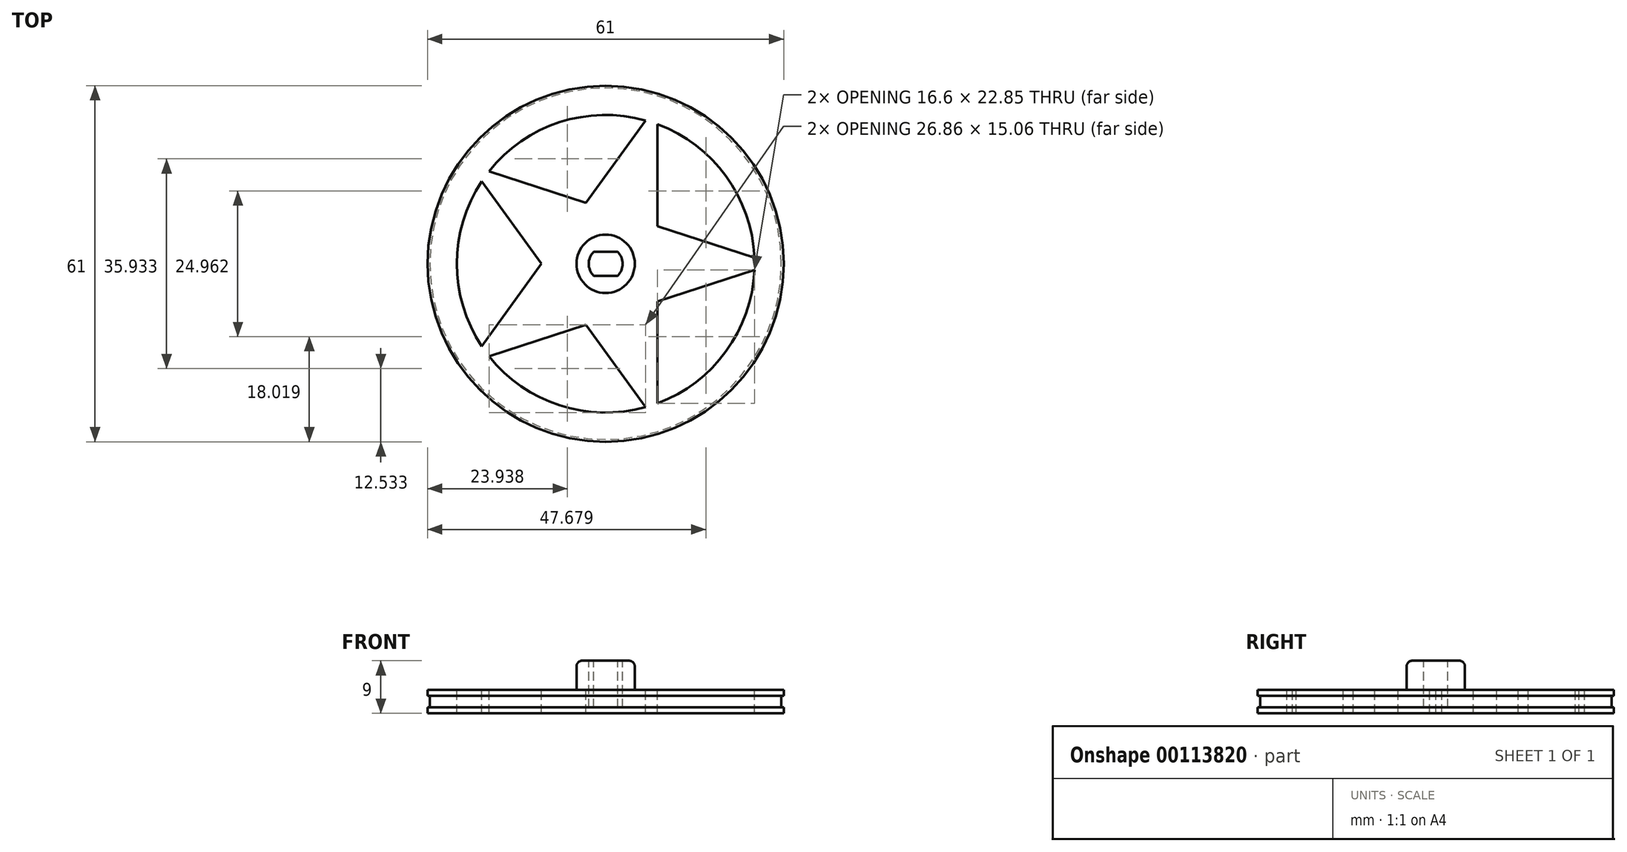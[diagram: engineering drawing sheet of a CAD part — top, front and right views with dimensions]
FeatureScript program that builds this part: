
annotation { "Feature Type Name" : "Feature", "Feature Type Description" : "" }
export const myFeature = defineFeature(function(context is Context, id is Id, definition is map)
    precondition{}
    {
        {
            var Q0;
            Q0=qCreatedBy(makeId("Top.planeOp"),FACE);
            var sketch = newSketch(context, id + "F0", { "sketchPlane" : qUnion([Q0])});
            skCircle(sketch, "E0", {"center": v(0, 0) * mm, "radius": 30.5 * mm});
            skSolve(sketch);
        }
        {
            var Q0;
            Q0 = qSketchRegion(id + "F0", true);
            extrude(context, id + "F1", {"entities" : qUnion([Q0]), "depth" : 4 * mm});
        }
        {
            var Q0;
            Q0=qCreatedBy(makeId("Top.planeOp"),FACE);
            cPlane(context, id + "F2", {"entities" : qUnion([Q0]), "cplaneType" : CPlaneType.OFFSET, "offset" : 1 * mm, "width" : 150 * mm, "height" : 150 * mm});
        }
        {
            var Q0;
            Q0=qCreatedBy(id+"F2.planeOp",FACE);
            var sketch = newSketch(context, id + "F3", { "sketchPlane" : qUnion([Q0])});
            skCircle(sketch, "E1.0", {"center": v(0, 0) * mm, "radius": 30.5 * mm});
            skCircle(sketch, "E2.0", {"center": v(0, 0) * mm, "radius": 30.1 * mm});
            skSolve(sketch);
        }
        {
            var Q0;
            Q0 = qSketchRegion(id + "F3", true);
            extrude(context, id + "F4", {"entities" : qUnion([Q0]), "operationType" : NewBodyOperationType.REMOVE, "depth" : 2 * mm});
        }
        {
            var Q0;
            Q0=makeQuery(id+"F1.opExtrude","CAP_FACE",FACE,{"disambiguationData":[OSD([sQuery(id+"F0.wireOp",EDGE,"E0")])],"isStart":false});
            var sketch = newSketch(context, id + "F5", { "sketchPlane" : qUnion([Q0])});
            skCircle(sketch, "E3", {"center": v(0, 0) * mm, "radius": 5 * mm});
            skSolve(sketch);
        }
        {
            var Q0;
            Q0 = qSketchRegion(id + "F5", true);
            extrude(context, id + "F6", {"entities" : qUnion([Q0]), "operationType" : NewBodyOperationType.ADD, "depth" : 5 * mm});
        }
        {
            var Q0;
            Q0=makeQuery(id+"F6.opExtrude","CAP_FACE",FACE,{"disambiguationData":[OSD([sQuery(id+"F5.wireOp",EDGE,"E3")])],"isStart":false});
            var sketch = newSketch(context, id + "F7", { "sketchPlane" : qUnion([Q0])});
            skArc(sketch, "E4", {"start": v(-2.05, 2.05) * mm, "mid": v(-2.9, 0) * mm, "end": v(-2.05, -2.05) * mm});
            skLineSegment(sketch, "E5", {"start": v(-2.05, 2.05) * mm, "end": v(2.05, 2.05) * mm});
            skLineSegment(sketch, "E6.MirrorCS", {"start": v(-2.05, -2.05) * mm, "end": v(2.05, -2.05) * mm});
            skArc(sketch, "E7.trimOffspring", {"start": v(2.05, -2.05) * mm, "mid": v(2.9, 0) * mm, "end": v(2.05, 2.05) * mm});
            skSolve(sketch);
        }
        {
            var Q0;
            Q0 = qSketchRegion(id + "F7", true);
            var Q1;
            Q1=qCreatedBy(id+"F2.planeOp",FACE);
            extrude(context, id + "F8", {"entities" : qUnion([Q0]), "operationType" : NewBodyOperationType.REMOVE, "endBound" : BoundingType.UP_TO_SURFACE, "oppositeDirection" : true, "endBoundEntityFace" : qUnion([Q1]), "depth" : 25 * mm});
        }
        {
            var Q0;
            Q0=makeQuery(id+"F1.opExtrude","CAP_FACE",FACE,{"disambiguationData":[OSD([sQuery(id+"F0.wireOp",EDGE,"E0")])],"isStart":false});
            var sketch = newSketch(context, id + "F9", { "sketchPlane" : qUnion([Q0])});
            skCircle(sketch, "E8.cCircle", {"center": v(0, 0) * mm, "radius": 25.5 * mm});
            skLineSegment(sketch, "E8.0", {"start": v(25.5, 0) * mm, "end": v(7.88, -24.25) * mm, "construction": true});
            skLineSegment(sketch, "E8.1", {"start": v(7.88, -24.25) * mm, "end": v(-20.63, -14.99) * mm, "construction": true});
            skLineSegment(sketch, "E8.2", {"start": v(-20.63, -14.99) * mm, "end": v(-20.63, 14.99) * mm, "construction": true});
            skLineSegment(sketch, "E8.3", {"start": v(-20.63, 14.99) * mm, "end": v(7.88, 24.25) * mm, "construction": true});
            skLineSegment(sketch, "E8.4", {"start": v(7.88, 24.25) * mm, "end": v(25.5, 0) * mm, "construction": true});
            skLineSegment(sketch, "E9", {"start": v(7.88, 24.25) * mm, "end": v(7.88, 5.73) * mm, "construction": true});
            skLineSegment(sketch, "E10", {"start": v(-20.63, 14.99) * mm, "end": v(-9.74, 0) * mm, "construction": true});
            skLineSegment(sketch, "E11", {"start": v(-20.63, -14.99) * mm, "end": v(-9.74, 0) * mm, "construction": true});
            skLineSegment(sketch, "E12", {"start": v(-20.63, 14.99) * mm, "end": v(-3, 9.26) * mm, "construction": true});
            skLineSegment(sketch, "E13", {"start": v(-20.63, -14.99) * mm, "end": v(-3, -9.26) * mm, "construction": true});
            skLineSegment(sketch, "E14.trimOffspring", {"start": v(7.88, 5.73) * mm, "end": v(25.5, 0) * mm, "construction": true});
            skLineSegment(sketch, "E15.trimOffspring", {"start": v(7.88, -5.73) * mm, "end": v(7.88, -24.25) * mm, "construction": true});
            skLineSegment(sketch, "E16.trimOffspring", {"start": v(7.88, -5.73) * mm, "end": v(25.5, 0) * mm, "construction": true});
            skLineSegment(sketch, "E17.trimOffspring", {"start": v(-3, -9.26) * mm, "end": v(7.88, -24.25) * mm, "construction": true});
            skLineSegment(sketch, "E18.trimOffspring", {"start": v(-3, 9.26) * mm, "end": v(7.88, 24.25) * mm, "construction": true});
            skLineSegment(sketch, "E19.0", {"start": v(-23.25, 16.9) * mm, "end": v(-3.4, 10.44) * mm});
            skLineSegment(sketch, "E19.1", {"start": v(-23.25, 16.9) * mm, "end": v(-10.98, 0) * mm});
            skLineSegment(sketch, "E19.2", {"start": v(-3.4, 10.44) * mm, "end": v(8.88, 27.33) * mm});
            skLineSegment(sketch, "E19.3", {"start": v(-23.25, -16.9) * mm, "end": v(-10.98, 0) * mm});
            skLineSegment(sketch, "E19.4", {"start": v(-23.25, -16.9) * mm, "end": v(-3.4, -10.44) * mm});
            skLineSegment(sketch, "E19.5", {"start": v(-3.4, -10.44) * mm, "end": v(8.88, -27.33) * mm});
            skLineSegment(sketch, "E19.6", {"start": v(8.88, 27.33) * mm, "end": v(8.88, 6.45) * mm});
            skLineSegment(sketch, "E19.7", {"start": v(8.88, 6.45) * mm, "end": v(28.74, 0) * mm});
            skLineSegment(sketch, "E19.8", {"start": v(8.88, -6.45) * mm, "end": v(28.74, 0) * mm});
            skLineSegment(sketch, "E19.9", {"start": v(8.88, -6.45) * mm, "end": v(8.88, -27.33) * mm});
            skSolve(sketch);
        }
        {
            var Q0;
            {var subQ0=sQuery(id+"F9.wireOp",EDGE,"E19.2");var subQ1=sQuery(id+"F9.wireOp",EDGE,"E8.cCircle");var subQ2=makeQuery(id+"F9.imprint","INTERSECT",VERTEX,{"derivedFrom":[subQ1,subQ0]});Q0=makeQuery(id+"F9.imprint","IMPRINT",FACE,{"disambiguationData":[TD([[makeQuery(id+"F9.imprint","IMPRINT",EDGE,{"disambiguationData":[TD([[subQ2,-1.0]])],"derivedFrom":subQ1}),1.0]])]});}
            var Q1;
            {var subQ0=sQuery(id+"F9.wireOp",EDGE,"E19.6");var subQ1=sQuery(id+"F9.wireOp",EDGE,"E8.cCircle");var subQ2=makeQuery(id+"F9.imprint","INTERSECT",VERTEX,{"derivedFrom":[subQ1,subQ0]});Q1=makeQuery(id+"F9.imprint","IMPRINT",FACE,{"disambiguationData":[TD([[makeQuery(id+"F9.imprint","IMPRINT",EDGE,{"disambiguationData":[TD([[subQ2,1.0]])],"derivedFrom":subQ1}),1.0]])]});}
            var Q2;
            {var subQ0=sQuery(id+"F9.wireOp",EDGE,"E19.9");var subQ1=sQuery(id+"F9.wireOp",EDGE,"E8.cCircle");var subQ2=makeQuery(id+"F9.imprint","INTERSECT",VERTEX,{"derivedFrom":[subQ1,subQ0]});Q2=makeQuery(id+"F9.imprint","IMPRINT",FACE,{"disambiguationData":[TD([[makeQuery(id+"F9.imprint","IMPRINT",EDGE,{"disambiguationData":[TD([[subQ2,-1.0]])],"derivedFrom":subQ1}),1.0]])]});}
            var Q3;
            {var subQ0=sQuery(id+"F9.wireOp",EDGE,"E19.4");var subQ1=sQuery(id+"F9.wireOp",EDGE,"E8.cCircle");var subQ2=makeQuery(id+"F9.imprint","INTERSECT",VERTEX,{"derivedFrom":[subQ1,subQ0]});Q3=makeQuery(id+"F9.imprint","IMPRINT",FACE,{"disambiguationData":[TD([[makeQuery(id+"F9.imprint","IMPRINT",EDGE,{"disambiguationData":[TD([[subQ2,-1.0]])],"derivedFrom":subQ1}),1.0]])]});}
            var Q4;
            {var subQ0=sQuery(id+"F9.wireOp",EDGE,"E19.1");var subQ1=sQuery(id+"F9.wireOp",EDGE,"E8.cCircle");var subQ2=makeQuery(id+"F9.imprint","INTERSECT",VERTEX,{"derivedFrom":[subQ1,subQ0]});Q4=makeQuery(id+"F9.imprint","IMPRINT",FACE,{"disambiguationData":[TD([[makeQuery(id+"F9.imprint","IMPRINT",EDGE,{"disambiguationData":[TD([[subQ2,-1.0]])],"derivedFrom":subQ1}),1.0]])]});}
            extrude(context, id + "F10", {"entities" : qUnion([Q0, Q1, Q2, Q3, Q4]), "operationType" : NewBodyOperationType.REMOVE, "oppositeDirection" : true, "depth" : 25 * mm});
        }
        {
            var Q0;
            Q0=makeQuery(id+"F6.opExtrude","CAP_EDGE",EDGE,{"disambiguationData":[OSD([sQuery(id+"F5.wireOp",EDGE,"E3")])],"isStart":false});
            var Q1;
            Q1=makeQuery(id+"F6.opExtrude","CAP_EDGE",EDGE,{"disambiguationData":[OSD([sQuery(id+"F5.wireOp",EDGE,"E3")])],"isStart":true});
            fillet(context, id + "F11", {"entities" : qUnion([Q0, Q1]), "radius" : 1 * mm, "tangentPropagation" : true, "allowEdgeOverflow" : false});
        }
    });
